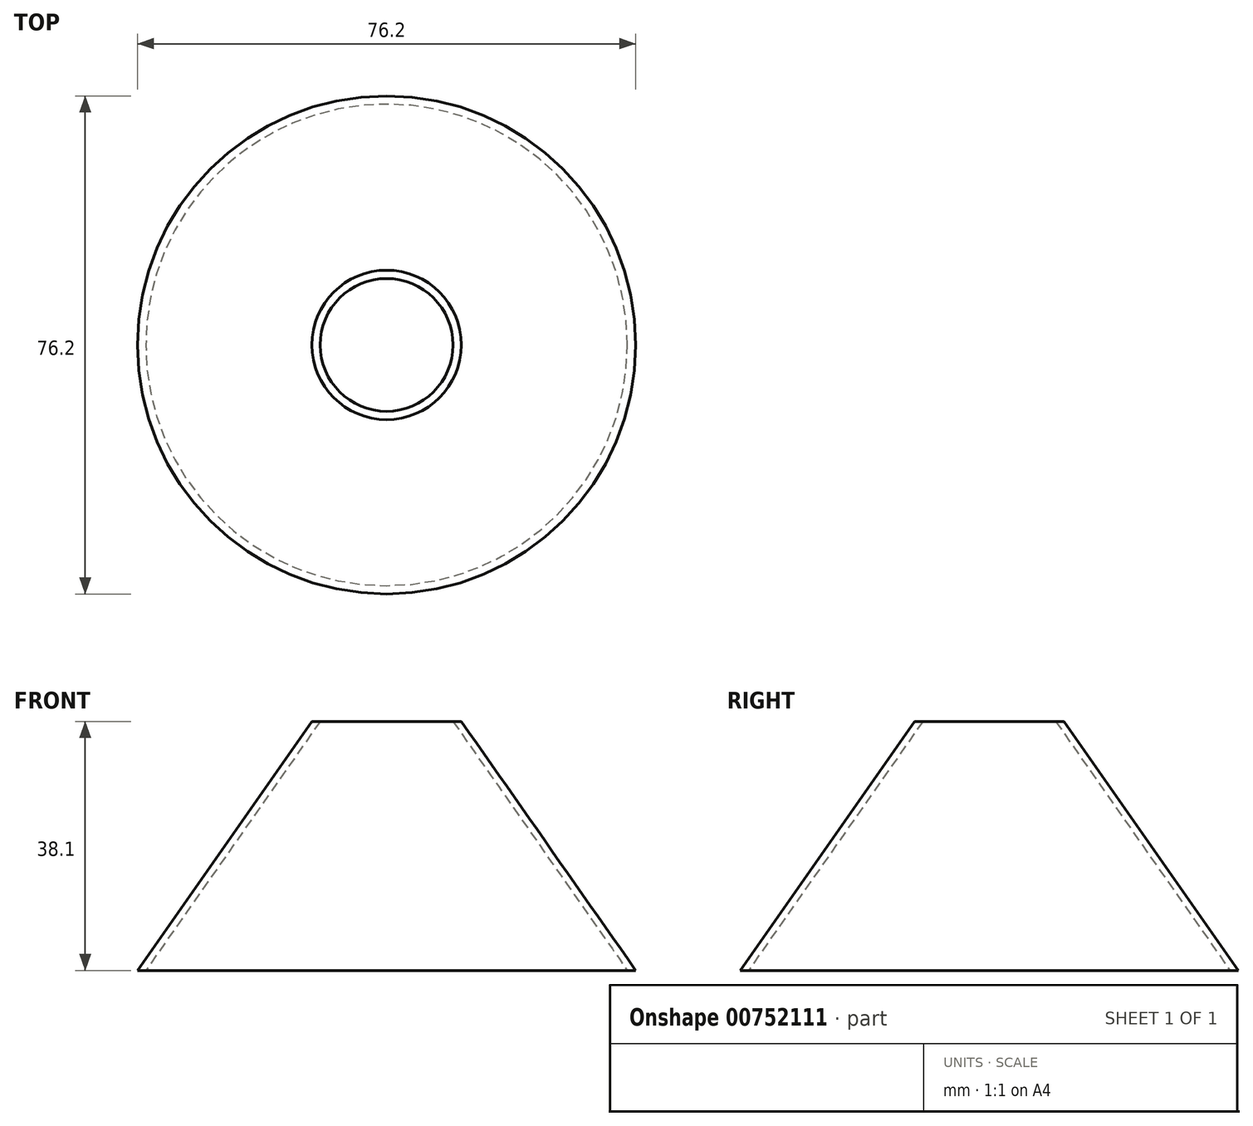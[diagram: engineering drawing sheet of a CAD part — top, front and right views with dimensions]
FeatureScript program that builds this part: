
annotation { "Feature Type Name" : "Feature", "Feature Type Description" : "" }
export const myFeature = defineFeature(function(context is Context, id is Id, definition is map)
    precondition{}
    {
        {
            var Q0;
            Q0=qCreatedBy(makeId("Front.planeOp"),FACE);
            var sketch = newSketch(context, id + "F0", { "sketchPlane" : qUnion([Q0])});
            skLineSegment(sketch, "E0", {"start": v(-11.43, 25.06) * mm, "end": v(-38.1, -13.04) * mm});
            skLineSegment(sketch, "E1", {"start": v(-38.1, -13.04) * mm, "end": v(-36.83, -13.04) * mm});
            skLineSegment(sketch, "E2", {"start": v(-36.83, -13.04) * mm, "end": v(-10.16, 25.06) * mm});
            skLineSegment(sketch, "E3", {"start": v(-11.43, 25.06) * mm, "end": v(-10.16, 25.06) * mm});
            skSolve(sketch);
        }
        {
            var Q0;
            Q0=qCreatedBy(makeId("Front.planeOp"),FACE);
            var sketch = newSketch(context, id + "F1", { "sketchPlane" : qUnion([Q0])});
            skLineSegment(sketch, "E4", {"start": v(0, 31.2) * mm, "end": v(0, -30.07) * mm});
            skSolve(sketch);
        }
        {
            var Q0;
            Q0=makeQuery(id+"F0.imprint","IMPRINT",FACE,{"disambiguationData":[TD([[makeQuery(id+"F0.imprint","IMPRINT",EDGE,{"derivedFrom":sQuery(id+"F0.wireOp",EDGE,"E0")}),1.0]])]});
            var Q1;
            Q1=sQuery(id+"F1.wireOp",EDGE,"E4");
            revolve(context, id + "F2", {"surfaceOperationType" : NewSurfaceOperationType.NEW, "entities" : qUnion([Q0]), "axis" : qUnion([Q1]), "revolveType" : RevolveType.FULL});
        }
    });
